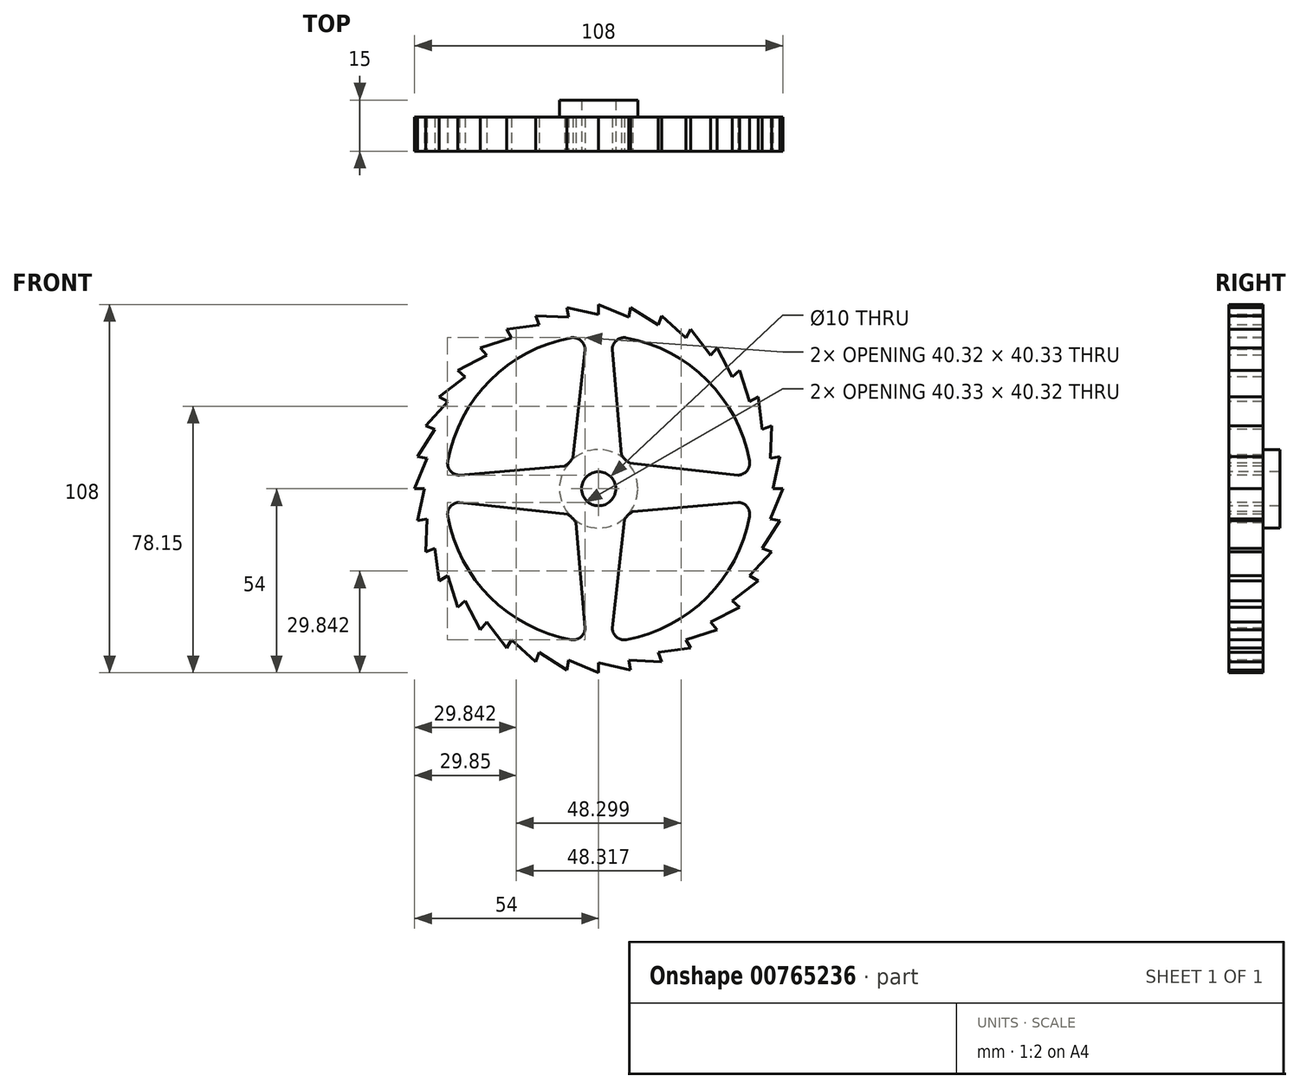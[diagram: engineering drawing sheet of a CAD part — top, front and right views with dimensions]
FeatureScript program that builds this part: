
annotation { "Feature Type Name" : "Feature", "Feature Type Description" : "" }
export const myFeature = defineFeature(function(context is Context, id is Id, definition is map)
    precondition{}
    {
        {
            var Q0;
            Q0=qCreatedBy(makeId("Front.planeOp"),FACE);
            var sketch = newSketch(context, id + "F0", { "sketchPlane" : qUnion([Q0])});
            skCircle(sketch, "E0", {"center": v(0, 0) * mm, "radius": 54 * mm, "construction": true});
            skCircle(sketch, "E1", {"center": v(0, 0) * mm, "radius": 51 * mm, "construction": true});
            skArc(sketch, "E2", {"start": v(-8.13, 44.26) * mm, "mid": v(-31.83, 31.81) * mm, "end": v(-44.26, 8.12) * mm});
            skCircle(sketch, "E3", {"center": v(0, 0) * mm, "radius": 5 * mm});
            skPoint(sketch, "E4.visualSharp", {"position": v(-4, 44.82) * mm});
            skArc(sketch, "E4.filletArc", {"start": v(-4, 40.82) * mm, "mid": v(-5.26, 43.5) * mm, "end": v(-8.13, 44.26) * mm});
            skPoint(sketch, "E5.visualSharp", {"position": v(-44.82, 3.98) * mm});
            skArc(sketch, "E5.filletArc", {"start": v(-44.26, 8.12) * mm, "mid": v(-43.5, 5.24) * mm, "end": v(-40.82, 3.98) * mm});
            skLineSegment(sketch, "E6", {"start": v(-4, 40.82) * mm, "end": v(-7.52, 9.13) * mm});
            skLineSegment(sketch, "E7", {"start": v(-40.82, 3.98) * mm, "end": v(-9.97, 6.68) * mm});
            skArc(sketch, "E8", {"start": v(-9.97, 6.68) * mm, "mid": v(-8.58, 7.74) * mm, "end": v(-7.52, 9.13) * mm});
            skLineSegment(sketch, "E9.1.0", {"start": v(-3.98, -40.82) * mm, "end": v(-6.68, -9.97) * mm});
            skArc(sketch, "E9.1.1", {"start": v(-6.68, -9.97) * mm, "mid": v(-7.74, -8.58) * mm, "end": v(-9.13, -7.52) * mm});
            skLineSegment(sketch, "E9.1.2", {"start": v(-40.82, -4) * mm, "end": v(-9.13, -7.52) * mm});
            skArc(sketch, "E9.1.3", {"start": v(-40.82, -4) * mm, "mid": v(-43.5, -5.26) * mm, "end": v(-44.26, -8.13) * mm});
            skArc(sketch, "E9.1.4", {"start": v(-44.26, -8.13) * mm, "mid": v(-31.81, -31.83) * mm, "end": v(-8.12, -44.26) * mm});
            skArc(sketch, "E9.1.5", {"start": v(-8.12, -44.26) * mm, "mid": v(-5.24, -43.5) * mm, "end": v(-3.98, -40.82) * mm});
            skLineSegment(sketch, "E9.2.0", {"start": v(40.82, -3.98) * mm, "end": v(9.97, -6.68) * mm});
            skArc(sketch, "E9.2.1", {"start": v(9.97, -6.68) * mm, "mid": v(8.58, -7.74) * mm, "end": v(7.52, -9.13) * mm});
            skLineSegment(sketch, "E9.2.2", {"start": v(4, -40.82) * mm, "end": v(7.52, -9.13) * mm});
            skArc(sketch, "E9.2.3", {"start": v(4, -40.82) * mm, "mid": v(5.26, -43.5) * mm, "end": v(8.13, -44.26) * mm});
            skArc(sketch, "E9.2.4", {"start": v(8.13, -44.26) * mm, "mid": v(31.83, -31.81) * mm, "end": v(44.26, -8.12) * mm});
            skArc(sketch, "E9.2.5", {"start": v(44.26, -8.12) * mm, "mid": v(43.5, -5.24) * mm, "end": v(40.82, -3.98) * mm});
            skLineSegment(sketch, "E9.3.0", {"start": v(3.98, 40.82) * mm, "end": v(6.68, 9.97) * mm});
            skArc(sketch, "E9.3.1", {"start": v(6.68, 9.97) * mm, "mid": v(7.74, 8.58) * mm, "end": v(9.13, 7.52) * mm});
            skLineSegment(sketch, "E9.3.2", {"start": v(40.82, 4) * mm, "end": v(9.13, 7.52) * mm});
            skArc(sketch, "E9.3.3", {"start": v(40.82, 4) * mm, "mid": v(43.5, 5.26) * mm, "end": v(44.26, 8.13) * mm});
            skArc(sketch, "E9.3.4", {"start": v(44.26, 8.13) * mm, "mid": v(31.81, 31.83) * mm, "end": v(8.12, 44.26) * mm});
            skArc(sketch, "E9.3.5", {"start": v(8.12, 44.26) * mm, "mid": v(5.24, 43.5) * mm, "end": v(3.98, 40.82) * mm});
            skCircle(sketch, "E10", {"center": v(0, 0) * mm, "radius": 11.5 * mm});
            skLineSegment(sketch, "E11", {"start": v(0, 51) * mm, "end": v(0, 54) * mm});
            skLineSegment(sketch, "E12", {"start": v(0, 54) * mm, "end": v(9.23, 50.16) * mm});
            skLineSegment(sketch, "E13.1.0", {"start": v(-9.38, 53.18) * mm, "end": v(0.38, 51) * mm});
            skLineSegment(sketch, "E13.1.1", {"start": v(-8.86, 50.23) * mm, "end": v(-9.38, 53.18) * mm});
            skLineSegment(sketch, "E13.2.0", {"start": v(-18.47, 50.74) * mm, "end": v(-8.48, 50.3) * mm});
            skLineSegment(sketch, "E13.2.1", {"start": v(-17.44, 47.92) * mm, "end": v(-18.47, 50.74) * mm});
            skLineSegment(sketch, "E13.3.0", {"start": v(-27, 46.77) * mm, "end": v(-17.08, 48.05) * mm});
            skLineSegment(sketch, "E13.3.1", {"start": v(-25.5, 44.17) * mm, "end": v(-27, 46.77) * mm});
            skLineSegment(sketch, "E13.4.0", {"start": v(-34.71, 41.37) * mm, "end": v(-25.17, 44.36) * mm});
            skLineSegment(sketch, "E13.4.1", {"start": v(-32.78, 39.07) * mm, "end": v(-34.71, 41.37) * mm});
            skLineSegment(sketch, "E13.5.0", {"start": v(-41.37, 34.71) * mm, "end": v(-32.49, 39.31) * mm});
            skLineSegment(sketch, "E13.5.1", {"start": v(-39.07, 32.78) * mm, "end": v(-41.37, 34.71) * mm});
            skLineSegment(sketch, "E13.6.0", {"start": v(-46.77, 27) * mm, "end": v(-38.82, 33.07) * mm});
            skLineSegment(sketch, "E13.6.1", {"start": v(-44.17, 25.5) * mm, "end": v(-46.77, 27) * mm});
            skLineSegment(sketch, "E13.7.0", {"start": v(-50.74, 18.47) * mm, "end": v(-43.97, 25.83) * mm});
            skLineSegment(sketch, "E13.7.1", {"start": v(-47.92, 17.44) * mm, "end": v(-50.74, 18.47) * mm});
            skLineSegment(sketch, "E13.8.0", {"start": v(-53.18, 9.38) * mm, "end": v(-47.8, 17.8) * mm});
            skLineSegment(sketch, "E13.8.1", {"start": v(-50.23, 8.86) * mm, "end": v(-53.18, 9.38) * mm});
            skLineSegment(sketch, "E13.9.0", {"start": v(-54, 0) * mm, "end": v(-50.16, 9.23) * mm});
            skLineSegment(sketch, "E13.9.1", {"start": v(-51, 0) * mm, "end": v(-54, 0) * mm});
            skLineSegment(sketch, "E13.10.0", {"start": v(-53.18, -9.38) * mm, "end": v(-51, 0.38) * mm});
            skLineSegment(sketch, "E13.10.1", {"start": v(-50.23, -8.86) * mm, "end": v(-53.18, -9.38) * mm});
            skLineSegment(sketch, "E13.11.0", {"start": v(-50.74, -18.47) * mm, "end": v(-50.3, -8.48) * mm});
            skLineSegment(sketch, "E13.11.1", {"start": v(-47.92, -17.44) * mm, "end": v(-50.74, -18.47) * mm});
            skLineSegment(sketch, "E13.12.0", {"start": v(-46.77, -27) * mm, "end": v(-48.05, -17.08) * mm});
            skLineSegment(sketch, "E13.12.1", {"start": v(-44.17, -25.5) * mm, "end": v(-46.77, -27) * mm});
            skLineSegment(sketch, "E13.13.0", {"start": v(-41.37, -34.71) * mm, "end": v(-44.36, -25.17) * mm});
            skLineSegment(sketch, "E13.13.1", {"start": v(-39.07, -32.78) * mm, "end": v(-41.37, -34.71) * mm});
            skLineSegment(sketch, "E13.14.0", {"start": v(-34.71, -41.37) * mm, "end": v(-39.31, -32.49) * mm});
            skLineSegment(sketch, "E13.14.1", {"start": v(-32.78, -39.07) * mm, "end": v(-34.71, -41.37) * mm});
            skLineSegment(sketch, "E13.15.0", {"start": v(-27, -46.77) * mm, "end": v(-33.07, -38.82) * mm});
            skLineSegment(sketch, "E13.15.1", {"start": v(-25.5, -44.17) * mm, "end": v(-27, -46.77) * mm});
            skLineSegment(sketch, "E13.16.0", {"start": v(-18.47, -50.74) * mm, "end": v(-25.83, -43.97) * mm});
            skLineSegment(sketch, "E13.16.1", {"start": v(-17.44, -47.92) * mm, "end": v(-18.47, -50.74) * mm});
            skLineSegment(sketch, "E13.17.0", {"start": v(-9.38, -53.18) * mm, "end": v(-17.8, -47.8) * mm});
            skLineSegment(sketch, "E13.17.1", {"start": v(-8.86, -50.23) * mm, "end": v(-9.38, -53.18) * mm});
            skLineSegment(sketch, "E13.18.0", {"start": v(0, -54) * mm, "end": v(-9.23, -50.16) * mm});
            skLineSegment(sketch, "E13.18.1", {"start": v(0, -51) * mm, "end": v(0, -54) * mm});
            skLineSegment(sketch, "E13.19.0", {"start": v(9.38, -53.18) * mm, "end": v(-0.38, -51) * mm});
            skLineSegment(sketch, "E13.19.1", {"start": v(8.86, -50.23) * mm, "end": v(9.38, -53.18) * mm});
            skLineSegment(sketch, "E13.20.0", {"start": v(18.47, -50.74) * mm, "end": v(8.48, -50.3) * mm});
            skLineSegment(sketch, "E13.20.1", {"start": v(17.44, -47.92) * mm, "end": v(18.47, -50.74) * mm});
            skLineSegment(sketch, "E13.21.0", {"start": v(27, -46.77) * mm, "end": v(17.08, -48.05) * mm});
            skLineSegment(sketch, "E13.21.1", {"start": v(25.5, -44.17) * mm, "end": v(27, -46.77) * mm});
            skLineSegment(sketch, "E13.22.0", {"start": v(34.71, -41.37) * mm, "end": v(25.17, -44.36) * mm});
            skLineSegment(sketch, "E13.22.1", {"start": v(32.78, -39.07) * mm, "end": v(34.71, -41.37) * mm});
            skLineSegment(sketch, "E13.23.0", {"start": v(41.37, -34.71) * mm, "end": v(32.49, -39.31) * mm});
            skLineSegment(sketch, "E13.23.1", {"start": v(39.07, -32.78) * mm, "end": v(41.37, -34.71) * mm});
            skLineSegment(sketch, "E13.24.0", {"start": v(46.77, -27) * mm, "end": v(38.82, -33.07) * mm});
            skLineSegment(sketch, "E13.24.1", {"start": v(44.17, -25.5) * mm, "end": v(46.77, -27) * mm});
            skLineSegment(sketch, "E13.25.0", {"start": v(50.74, -18.47) * mm, "end": v(43.97, -25.83) * mm});
            skLineSegment(sketch, "E13.25.1", {"start": v(47.92, -17.44) * mm, "end": v(50.74, -18.47) * mm});
            skLineSegment(sketch, "E13.26.0", {"start": v(53.18, -9.38) * mm, "end": v(47.8, -17.8) * mm});
            skLineSegment(sketch, "E13.26.1", {"start": v(50.23, -8.86) * mm, "end": v(53.18, -9.38) * mm});
            skLineSegment(sketch, "E13.27.0", {"start": v(54, 0) * mm, "end": v(50.16, -9.23) * mm});
            skLineSegment(sketch, "E13.27.1", {"start": v(51, 0) * mm, "end": v(54, 0) * mm});
            skLineSegment(sketch, "E13.28.0", {"start": v(53.18, 9.38) * mm, "end": v(51, -0.38) * mm});
            skLineSegment(sketch, "E13.28.1", {"start": v(50.23, 8.86) * mm, "end": v(53.18, 9.38) * mm});
            skLineSegment(sketch, "E13.29.0", {"start": v(50.74, 18.47) * mm, "end": v(50.3, 8.48) * mm});
            skLineSegment(sketch, "E13.29.1", {"start": v(47.92, 17.44) * mm, "end": v(50.74, 18.47) * mm});
            skLineSegment(sketch, "E13.30.0", {"start": v(46.77, 27) * mm, "end": v(48.05, 17.08) * mm});
            skLineSegment(sketch, "E13.30.1", {"start": v(44.17, 25.5) * mm, "end": v(46.77, 27) * mm});
            skLineSegment(sketch, "E13.31.0", {"start": v(41.37, 34.71) * mm, "end": v(44.36, 25.17) * mm});
            skLineSegment(sketch, "E13.31.1", {"start": v(39.07, 32.78) * mm, "end": v(41.37, 34.71) * mm});
            skLineSegment(sketch, "E13.32.0", {"start": v(34.71, 41.37) * mm, "end": v(39.31, 32.49) * mm});
            skLineSegment(sketch, "E13.32.1", {"start": v(32.78, 39.07) * mm, "end": v(34.71, 41.37) * mm});
            skLineSegment(sketch, "E13.33.0", {"start": v(27, 46.77) * mm, "end": v(33.07, 38.82) * mm});
            skLineSegment(sketch, "E13.33.1", {"start": v(25.5, 44.17) * mm, "end": v(27, 46.77) * mm});
            skLineSegment(sketch, "E13.34.0", {"start": v(18.47, 50.74) * mm, "end": v(25.83, 43.97) * mm});
            skLineSegment(sketch, "E13.34.1", {"start": v(17.44, 47.92) * mm, "end": v(18.47, 50.74) * mm});
            skLineSegment(sketch, "E13.35.0", {"start": v(9.38, 53.18) * mm, "end": v(17.8, 47.8) * mm});
            skLineSegment(sketch, "E13.35.1", {"start": v(8.86, 50.23) * mm, "end": v(9.38, 53.18) * mm});
            skSolve(sketch);
        }
        {
            var Q0;
            Q0=makeQuery(id+"F0.imprint","IMPRINT",FACE,{"disambiguationData":[TD([[makeQuery(id+"F0.imprint","IMPRINT",EDGE,{"derivedFrom":sQuery(id+"F0.wireOp",EDGE,"E2")}),-1.0]])]});
            extrude(context, id + "F1", {"entities" : qUnion([Q0]), "oppositeDirection" : true, "depth" : 10 * mm, "offsetDistance" : 25 * mm});
        }
        {
            var Q0;
            Q0=makeQuery(id+"F0.imprint","IMPRINT",FACE,{"disambiguationData":[TD([[makeQuery(id+"F0.imprint","IMPRINT",EDGE,{"derivedFrom":sQuery(id+"F0.wireOp",EDGE,"E3")}),-1.0]])]});
            extrude(context, id + "F2", {"entities" : qUnion([Q0]), "operationType" : NewBodyOperationType.ADD, "oppositeDirection" : true, "depth" : 15 * mm, "offsetDistance" : 25 * mm});
        }
    });
